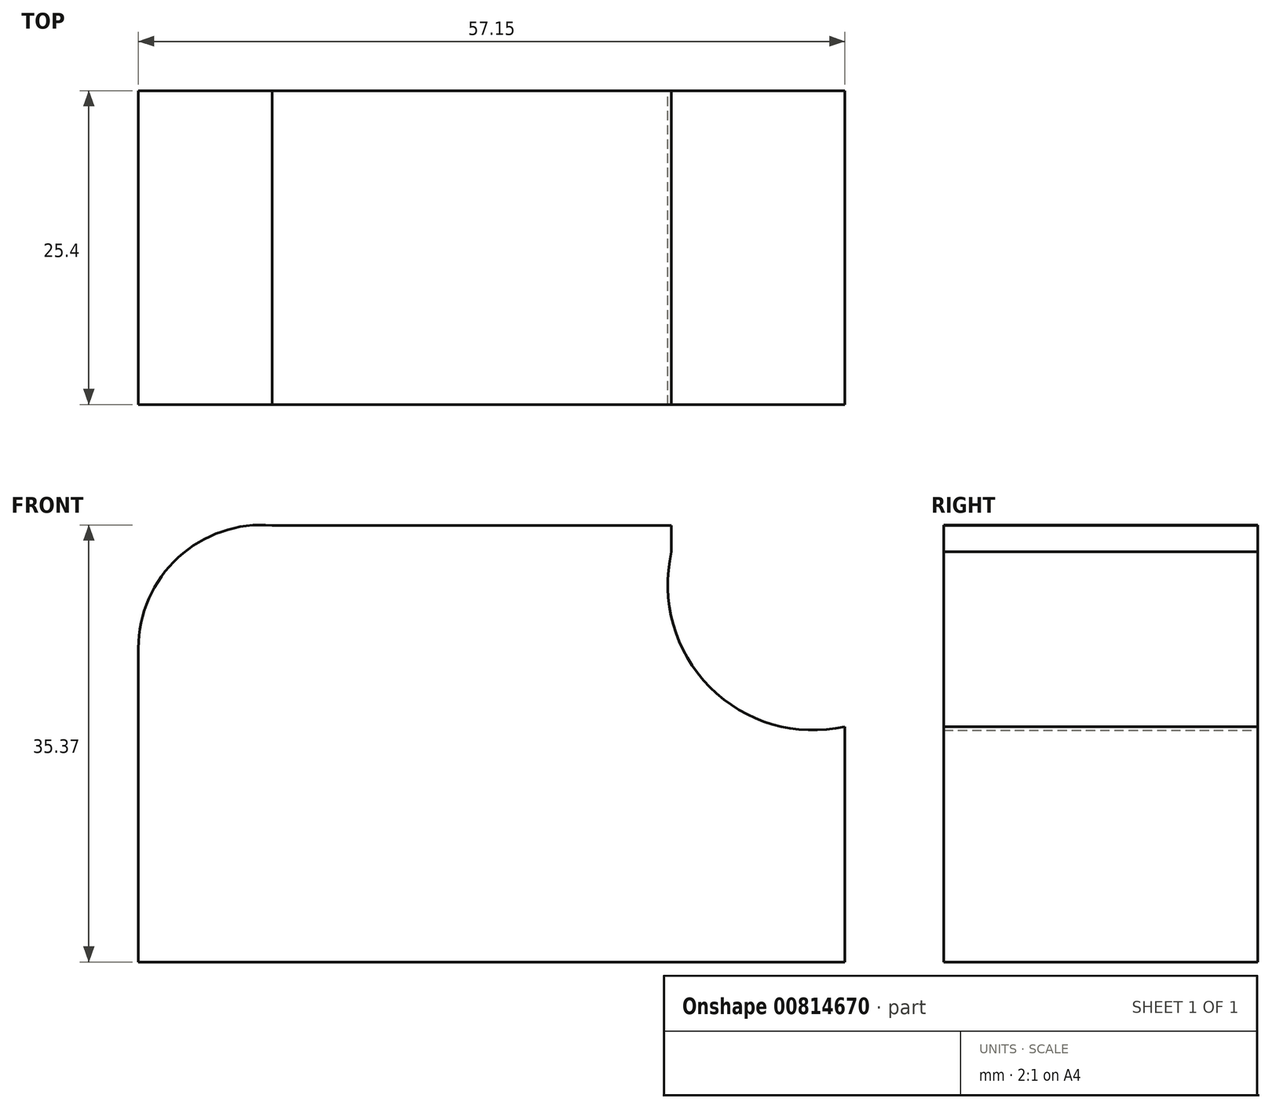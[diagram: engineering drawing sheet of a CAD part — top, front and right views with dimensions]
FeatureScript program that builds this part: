
annotation { "Feature Type Name" : "Feature", "Feature Type Description" : "" }
export const myFeature = defineFeature(function(context is Context, id is Id, definition is map)
    precondition{}
    {
        {
            var Q0;
            Q0=qCreatedBy(makeId("Front.planeOp"),FACE);
            var sketch = newSketch(context, id + "F0", { "sketchPlane" : qUnion([Q0])});
            skLineSegment(sketch, "E0", {"start": v(0, 0) * mm, "end": v(57.15, 0) * mm});
            skLineSegment(sketch, "E1", {"start": v(0, 0) * mm, "end": v(0, 25.4) * mm});
            skLineSegment(sketch, "E2", {"start": v(57.15, 0) * mm, "end": v(57.15, 19.05) * mm});
            skArc(sketch, "E3", {"start": v(0, 25.4) * mm, "mid": v(3.22, 32.74) * mm, "end": v(10.8, 35.33) * mm});
            skArc(sketch, "E4", {"start": v(43.12, 33.2) * mm, "mid": v(46.22, 22.24) * mm, "end": v(57.15, 19.05) * mm});
            skLineSegment(sketch, "E5", {"start": v(10.8, 35.33) * mm, "end": v(43.12, 35.33) * mm});
            skLineSegment(sketch, "E6", {"start": v(43.12, 35.33) * mm, "end": v(43.12, 33.2) * mm});
            skSolve(sketch);
        }
        {
            var Q0;
            Q0 = qSketchRegion(id + "F0", true);
            extrude(context, id + "F1", {"entities" : qUnion([Q0]), "depth" : 25.4 * mm, "offsetDistance" : 25.4 * mm});
        }
    });
